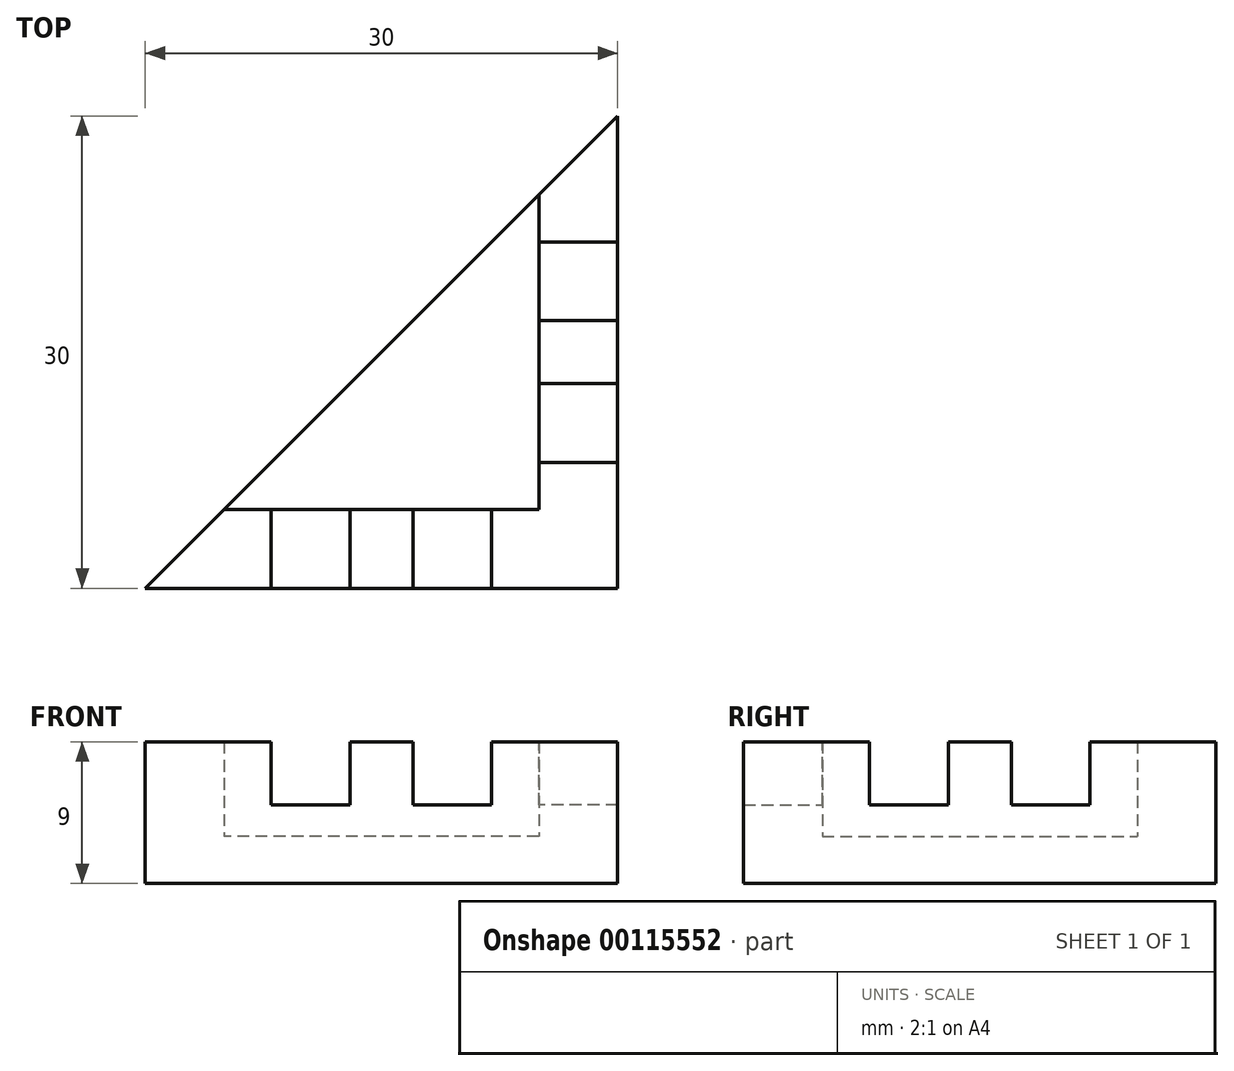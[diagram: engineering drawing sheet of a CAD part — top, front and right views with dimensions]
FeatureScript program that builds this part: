
annotation { "Feature Type Name" : "Feature", "Feature Type Description" : "" }
export const myFeature = defineFeature(function(context is Context, id is Id, definition is map)
    precondition{}
    {
        {
            var Q0;
            Q0=qCreatedBy(makeId("Top.planeOp"),FACE);
            var sketch = newSketch(context, id + "F0", { "sketchPlane" : qUnion([Q0])});
            skLineSegment(sketch, "E0", {"start": v(0, 0) * mm, "end": v(30, 0) * mm});
            skLineSegment(sketch, "E1", {"start": v(30, 0) * mm, "end": v(30, 30) * mm});
            skLineSegment(sketch, "E2", {"start": v(30, 30) * mm, "end": v(0, 0) * mm});
            skSolve(sketch);
        }
        {
            var Q0;
            Q0=makeQuery(id+"F0.imprint","IMPRINT",FACE,{"disambiguationData":[TD([[makeQuery(id+"F0.imprint","IMPRINT",EDGE,{"derivedFrom":sQuery(id+"F0.wireOp",EDGE,"E0")}),1.0]])]});
            extrude(context, id + "F1", {"entities" : qUnion([Q0]), "depth" : 3 * mm});
        }
        {
            var Q0;
            Q0=makeQuery(id+"F1.opExtrude","CAP_FACE",FACE,{"disambiguationData":[OSD([sQuery(id+"F0.wireOp",EDGE,"E0"),sQuery(id+"F0.wireOp",EDGE,"E1"),sQuery(id+"F0.wireOp",EDGE,"E2")])],"isStart":false});
            var sketch = newSketch(context, id + "F2", { "sketchPlane" : qUnion([Q0])});
            skLineSegment(sketch, "E3", {"start": v(0, 0) * mm, "end": v(25, 0) * mm});
            skLineSegment(sketch, "E4", {"start": v(25, 5) * mm, "end": v(5, 5) * mm});
            skLineSegment(sketch, "E5", {"start": v(25, 5) * mm, "end": v(25, 25) * mm});
            skSolve(sketch);
        }
        {
            var Q0;
            Q0 = qSketchRegion(id + "F2", true);
            var Q1;
            {var subQ2=sQuery(id+"F2.wireOp",EDGE,"E3");Q1=makeQuery(id+"F2.imprint","IMPRINT",FACE,{"disambiguationData":[TD([[makeQuery(id+"F2.imprint","IMPRINT",EDGE,{"derivedFrom":subQ2}),1.0]])]});}
            extrude(context, id + "F3", {"entities" : qUnion([Q0, Q1]), "operationType" : NewBodyOperationType.ADD, "depth" : 6 * mm});
        }
        {
            var Q0;
            Q0=makeQuery(id+"F3.opExtrude","CAP_FACE",FACE,{"disambiguationData":[OSD([sQuery(id+"F0.wireOp",EDGE,"E0"),sQuery(id+"F0.wireOp",EDGE,"E1"),sQuery(id+"F0.wireOp",EDGE,"E2"),sQuery(id+"F2.wireOp",EDGE,"E3"),sQuery(id+"F2.wireOp",EDGE,"E4"),sQuery(id+"F2.wireOp",EDGE,"E5")])],"isStart":false});
            var sketch = newSketch(context, id + "F4", { "sketchPlane" : qUnion([Q0])});
            skLineSegment(sketch, "E6", {"start": v(0, 0) * mm, "end": v(8, 0) * mm});
            skLineSegment(sketch, "E7.bottom", {"start": v(8, 0) * mm, "end": v(13, 0) * mm});
            skLineSegment(sketch, "E7.top", {"start": v(8, 5) * mm, "end": v(13, 5) * mm});
            skLineSegment(sketch, "E7.left", {"start": v(8, 0) * mm, "end": v(8, 5) * mm});
            skLineSegment(sketch, "E7.right", {"start": v(13, 0) * mm, "end": v(13, 5) * mm});
            skLineSegment(sketch, "E8", {"start": v(13, 0) * mm, "end": v(17, 0) * mm});
            skLineSegment(sketch, "E9.bottom", {"start": v(17, 0) * mm, "end": v(22, 0) * mm});
            skLineSegment(sketch, "E9.top", {"start": v(17, 5) * mm, "end": v(22, 5) * mm});
            skLineSegment(sketch, "E9.left", {"start": v(17, 0) * mm, "end": v(17, 5) * mm});
            skLineSegment(sketch, "E9.right", {"start": v(22, 0) * mm, "end": v(22, 5) * mm});
            skLineSegment(sketch, "E10", {"start": v(30, 30) * mm, "end": v(30, 22) * mm});
            skLineSegment(sketch, "E11.bottom", {"start": v(30, 22) * mm, "end": v(25, 22) * mm});
            skLineSegment(sketch, "E11.top", {"start": v(30, 17) * mm, "end": v(25, 17) * mm});
            skLineSegment(sketch, "E11.left", {"start": v(30, 22) * mm, "end": v(30, 17) * mm});
            skLineSegment(sketch, "E11.right", {"start": v(25, 22) * mm, "end": v(25, 17) * mm});
            skLineSegment(sketch, "E12", {"start": v(30, 17) * mm, "end": v(30, 13) * mm});
            skLineSegment(sketch, "E13.bottom", {"start": v(30, 13) * mm, "end": v(25, 13) * mm});
            skLineSegment(sketch, "E13.top", {"start": v(30, 8) * mm, "end": v(25, 8) * mm});
            skLineSegment(sketch, "E13.left", {"start": v(30, 13) * mm, "end": v(30, 8) * mm});
            skLineSegment(sketch, "E13.right", {"start": v(25, 13) * mm, "end": v(25, 8) * mm});
            skSolve(sketch);
        }
        {
            var Q0;
            Q0=makeQuery(id+"F4.imprint","IMPRINT",FACE,{"disambiguationData":[TD([[makeQuery(id+"F4.imprint","IMPRINT",EDGE,{"derivedFrom":sQuery(id+"F4.wireOp",EDGE,"E7.bottom")}),1.0]])]});
            var Q1;
            Q1=makeQuery(id+"F4.imprint","IMPRINT",FACE,{"disambiguationData":[TD([[makeQuery(id+"F4.imprint","IMPRINT",EDGE,{"derivedFrom":sQuery(id+"F4.wireOp",EDGE,"E9.bottom")}),1.0]])]});
            var Q2;
            Q2=makeQuery(id+"F4.imprint","IMPRINT",FACE,{"disambiguationData":[TD([[makeQuery(id+"F4.imprint","IMPRINT",EDGE,{"derivedFrom":sQuery(id+"F4.wireOp",EDGE,"E13.bottom")}),1.0]])]});
            var Q3;
            Q3=makeQuery(id+"F4.imprint","IMPRINT",FACE,{"disambiguationData":[TD([[makeQuery(id+"F4.imprint","IMPRINT",EDGE,{"derivedFrom":sQuery(id+"F4.wireOp",EDGE,"E11.bottom")}),1.0]])]});
            extrude(context, id + "F5", {"entities" : qUnion([Q0, Q1, Q2, Q3]), "operationType" : NewBodyOperationType.REMOVE, "oppositeDirection" : true, "depth" : 4 * mm});
        }
        {
            var Q0;
            Q0=makeQuery(id+"F1.opExtrude","SWEPT_BODY",BODY,{"disambiguationData":[OSD([sQuery(id+"F0.wireOp",EDGE,"E0"),sQuery(id+"F0.wireOp",EDGE,"E1"),sQuery(id+"F0.wireOp",EDGE,"E2")])]});
            transform(context, id + "F6", {"entities" : qUnion([Q0]), "transformType" : TransformType.TRANSLATION_3D, "dx" : 0 * mm, "dy" : 0 * mm, "dz" : 0 * mm, "makeCopy" : true});
        }
    });
